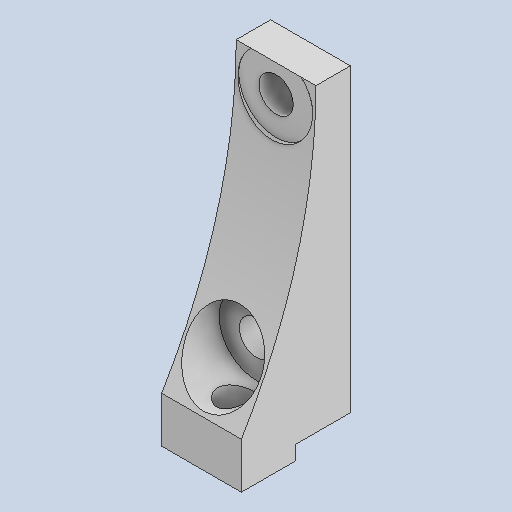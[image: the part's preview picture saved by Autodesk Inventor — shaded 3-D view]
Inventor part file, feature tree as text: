
AUTODESK INVENTOR PART (.ipt)
format: ipt  version: 2022 (Build 260153070, 153G)  size: 165,888 bytes
history: native  units: in
note: dims shown in document units (in); Inventor stores cm internally (conversion verified against a paired STEP export)
features: extrude x6, sketch x4, reference x2, other x2
ambient origin geometry x8: Origin, YZ Plane, XZ Plane, XY Plane, X Axis, Y Axis, Z Axis, Center Point
bodies: Solid1 (feature_tree)
feature tree (14):
  extrude  "Extrusion1"  Depth=0.1368in
  extrude  "Extrusion2"  Depth=0.1368in
  sketch  "Sketch3"  dims[d4=0.374in d5=0.0in d6=0.1181in]
  extrude  "Extrusion3"  Depth=0.1181in
  extrude  "Extrusion4"  Depth=0.3937in TaperAngle=0.0deg
  sketch  "Sketch4"  dims[d7=0.1575in d8=0.3937in d9=0.0in d10=0.3115in d11=0.0in d12=0.0492in d13=0.0in d14=0.1518in d15=0.0915in d16=0.1083in d17=0.2559in d18=0.1885in d19=0.0in d20=0.249in d21=0.0in]
  extrude  "Extrusion5"  Depth=0.3937in TaperAngle=0.0deg
  extrude  "Extrusion6"  Depth=0.3937in TaperAngle=0.0deg
  sketch  "Sketch1"  dims[d0=1.0807in d1=0.1368in]
  reference  "Reference1"
  reference  "Reference2"
  sketch  "Sketch2"  dims[d2=0.0945in d3=0.1368in]
  other  "Assembly1"
  other  "TT motor output:1"
